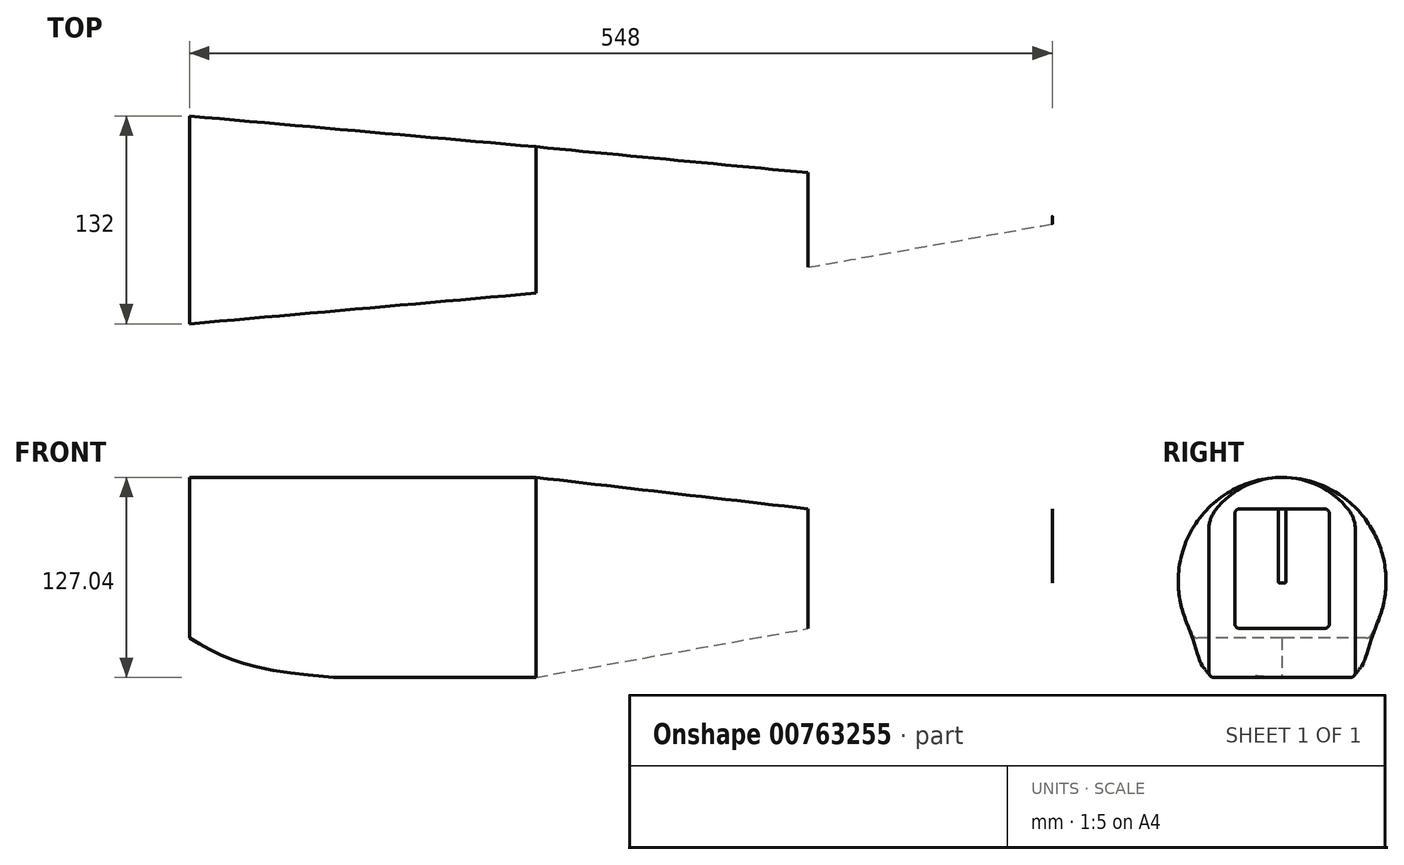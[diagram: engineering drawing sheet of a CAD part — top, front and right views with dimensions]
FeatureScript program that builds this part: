
annotation { "Feature Type Name" : "Feature", "Feature Type Description" : "" }
export const myFeature = defineFeature(function(context is Context, id is Id, definition is map)
    precondition{}
    {
        {
            var Q0;
            Q0=qCreatedBy(makeId("Front.planeOp"),FACE);
            var sketch = newSketch(context, id + "F0", { "sketchPlane" : qUnion([Q0])});
            skLineSegment(sketch, "E0", {"start": v(-298.93, 72.07) * mm, "end": v(-78.93, 72.07) * mm});
            skLineSegment(sketch, "E1", {"start": v(-298.93, 72.07) * mm, "end": v(-298.93, -29.93) * mm});
            skLineSegment(sketch, "E2", {"start": v(-78.93, 72.07) * mm, "end": v(-78.93, -54.93) * mm});
            skLineSegment(sketch, "E3", {"start": v(94.07, 52.07) * mm, "end": v(94.07, -23.93) * mm});
            skLineSegment(sketch, "E4", {"start": v(249.07, 52.07) * mm, "end": v(249.07, 5.07) * mm});
            skLineSegment(sketch, "E5", {"start": v(249.07, 5.07) * mm, "end": v(94.07, -23.93) * mm});
            skLineSegment(sketch, "E6", {"start": v(94.07, -23.93) * mm, "end": v(-78.93, -54.93) * mm});
            skLineSegment(sketch, "E7", {"start": v(-78.93, 72.07) * mm, "end": v(94.07, 52.07) * mm});
            skLineSegment(sketch, "E8", {"start": v(249.07, 52.07) * mm, "end": v(94.07, 52.07) * mm});
            skLineSegment(sketch, "E9", {"start": v(-78.93, 72.07) * mm, "end": v(94.07, 72.07) * mm, "construction": true});
            skLineSegment(sketch, "E10", {"start": v(94.07, 72.07) * mm, "end": v(249.07, 72.07) * mm, "construction": true});
            skLineSegment(sketch, "E11", {"start": v(94.07, 52.07) * mm, "end": v(94.07, 72.07) * mm, "construction": true});
            skLineSegment(sketch, "E12", {"start": v(249.07, 52.07) * mm, "end": v(249.07, 72.07) * mm, "construction": true});
            skLineSegment(sketch, "E13", {"start": v(-208.93, -54.93) * mm, "end": v(-208.93, -54.83) * mm, "construction": true});
            skFitSpline(sketch, "E14", {"points": [v(-298.93, -29.93) * mm, v(-277.86, -41.2) * mm, v(-246.75, -50.26) * mm, v(-207.1, -54.93) * mm, v(-204.2, -54.93) * mm, v(-200.61, -54.93) * mm, v(-196.68, -54.93) * mm, v(-192.58, -54.93) * mm, v(-78.93, -54.93) * mm], "startDerivative": vector(147.7, -86.05) * mm, "endDerivative": vector(505, 0.02) * mm});
            skLineSegment(sketch, "E15", {"start": v(-298.93, 6.07) * mm, "end": v(249.07, 6.07) * mm, "construction": true});
            skSolve(sketch);
        }
        {
            var Q0;
            Q0=sQuery(id+"F0.wireOp",EDGE,"E1");
            cPlane(context, id + "F1", {"entities" : qUnion([Q0]), "cplaneType" : CPlaneType.LINE_ANGLE, "offset" : 25 * mm, "angle" : 0 * degree, "width" : 150 * mm, "height" : 150 * mm});
        }
        {
            var Q0;
            Q0=sQuery(id+"F0.wireOp",EDGE,"E2");
            cPlane(context, id + "F2", {"entities" : qUnion([Q0]), "cplaneType" : CPlaneType.LINE_ANGLE, "offset" : 25 * mm, "angle" : 0 * degree, "width" : 150 * mm, "height" : 150 * mm});
        }
        {
            var Q0;
            Q0=sQuery(id+"F0.wireOp",EDGE,"E3");
            cPlane(context, id + "F3", {"entities" : qUnion([Q0]), "cplaneType" : CPlaneType.LINE_ANGLE, "offset" : 25 * mm, "angle" : 0 * degree, "width" : 150 * mm, "height" : 150 * mm});
        }
        {
            var Q0;
            Q0=qCreatedBy(id+"F1.planeOp",FACE);
            var sketch = newSketch(context, id + "F4", { "sketchPlane" : qUnion([Q0])});
            skArc(sketch, "E16", {"start": v(56.22, -28.5) * mm, "mid": v(42.66, 56.42) * mm, "end": v(-43.34, 55.84) * mm});
            skLineSegment(sketch, "E17", {"start": v(-53.67, -29.93) * mm, "end": v(53.67, -29.93) * mm});
            skPoint(sketch, "E18.visualSharp", {"position": v(55.32, -29.93) * mm});
            skArc(sketch, "E18.filletArc", {"start": v(53.67, -29.93) * mm, "mid": v(55.13, -29.55) * mm, "end": v(56.22, -28.5) * mm});
            skPoint(sketch, "E19.visualSharp", {"position": v(-55.32, -29.93) * mm});
            skArc(sketch, "E19.filletArc", {"start": v(-56.22, -28.5) * mm, "mid": v(-55.13, -29.55) * mm, "end": v(-53.67, -29.93) * mm});
            skArc(sketch, "E20", {"start": v(-43.34, 55.84) * mm, "mid": v(-65.24, 16.03) * mm, "end": v(-56.22, -28.5) * mm});
            skArc(sketch, "E21.MirrorCS", {"start": v(43.34, 55.84) * mm, "mid": v(65.24, 16.03) * mm, "end": v(56.22, -28.5) * mm});
            skLineSegment(sketch, "E22", {"start": v(-66, 6.07) * mm, "end": v(66, 6.07) * mm, "construction": true});
            skSolve(sketch);
        }
        {
            var Q0;
            Q0=qCreatedBy(id+"F2.planeOp",FACE);
            var sketch = newSketch(context, id + "F5", { "sketchPlane" : qUnion([Q0])});
            skLineSegment(sketch, "E23.top", {"start": v(43.5, -54.93) * mm, "end": v(-43.5, -54.93) * mm});
            skLineSegment(sketch, "E23.left", {"start": v(46.5, 39.09) * mm, "end": v(46.5, -51.93) * mm});
            skLineSegment(sketch, "E23.right", {"start": v(-46.5, 39.09) * mm, "end": v(-46.5, -51.93) * mm});
            skPoint(sketch, "E23.middle", {"position": v(0, -4.93) * mm});
            skArc(sketch, "E24", {"start": v(42.3, 51.35) * mm, "mid": v(0, 72.07) * mm, "end": v(-42.3, 51.35) * mm});
            skPoint(sketch, "E25.visualSharp", {"position": v(46.5, 45.07) * mm});
            skArc(sketch, "E25.filletArc", {"start": v(46.5, 39.09) * mm, "mid": v(45.42, 45.57) * mm, "end": v(42.3, 51.35) * mm});
            skPoint(sketch, "E26.visualSharp", {"position": v(46.5, -54.93) * mm});
            skArc(sketch, "E26.filletArc", {"start": v(43.5, -54.93) * mm, "mid": v(45.62, -54.06) * mm, "end": v(46.5, -51.93) * mm});
            skPoint(sketch, "E27.visualSharp", {"position": v(-46.5, -54.93) * mm});
            skArc(sketch, "E27.filletArc", {"start": v(-46.5, -51.93) * mm, "mid": v(-45.62, -54.06) * mm, "end": v(-43.5, -54.93) * mm});
            skPoint(sketch, "E28.visualSharp", {"position": v(-46.5, 45.07) * mm});
            skArc(sketch, "E28.filletArc", {"start": v(-42.3, 51.35) * mm, "mid": v(-45.42, 45.57) * mm, "end": v(-46.5, 39.09) * mm});
            skLineSegment(sketch, "E29", {"start": v(46.5, 6.07) * mm, "end": v(-46.5, 6.07) * mm, "construction": true});
            skSolve(sketch);
        }
        {
            var Q0;
            Q0=qCreatedBy(id+"F3.planeOp",FACE);
            var sketch = newSketch(context, id + "F6", { "sketchPlane" : qUnion([Q0])});
            skLineSegment(sketch, "E30.bottom", {"start": v(27, 52.07) * mm, "end": v(-27, 52.07) * mm});
            skLineSegment(sketch, "E30.top", {"start": v(27, -23.93) * mm, "end": v(-27, -23.93) * mm});
            skLineSegment(sketch, "E30.left", {"start": v(30, 49.07) * mm, "end": v(30, -20.93) * mm});
            skLineSegment(sketch, "E30.right", {"start": v(-30, 49.07) * mm, "end": v(-30, -20.93) * mm});
            skPoint(sketch, "E30.middle", {"position": v(0, 14.07) * mm});
            skPoint(sketch, "E31.visualSharp", {"position": v(30, 52.07) * mm});
            skArc(sketch, "E31.filletArc", {"start": v(30, 49.07) * mm, "mid": v(29.12, 51.19) * mm, "end": v(27, 52.07) * mm});
            skPoint(sketch, "E32.visualSharp", {"position": v(-30, 52.07) * mm});
            skArc(sketch, "E32.filletArc", {"start": v(-27, 52.07) * mm, "mid": v(-29.12, 51.19) * mm, "end": v(-30, 49.07) * mm});
            skPoint(sketch, "E33.visualSharp", {"position": v(30, -23.93) * mm});
            skArc(sketch, "E33.filletArc", {"start": v(27, -23.93) * mm, "mid": v(29.12, -23.06) * mm, "end": v(30, -20.93) * mm});
            skPoint(sketch, "E34.visualSharp", {"position": v(-30, -23.93) * mm});
            skArc(sketch, "E34.filletArc", {"start": v(-30, -20.93) * mm, "mid": v(-29.12, -23.06) * mm, "end": v(-27, -23.93) * mm});
            skLineSegment(sketch, "E35", {"start": v(30, 6.07) * mm, "end": v(-30, 6.07) * mm, "construction": true});
            skSolve(sketch);
        }
        {
            var Q0;
            Q0=sQuery(id+"F0.wireOp",EDGE,"E4");
            cPlane(context, id + "F7", {"entities" : qUnion([Q0]), "cplaneType" : CPlaneType.LINE_ANGLE, "offset" : 25 * mm, "angle" : 0 * degree, "width" : 150 * mm, "height" : 150 * mm});
        }
        {
            var Q0;
            Q0=qCreatedBy(id+"F7.planeOp",FACE);
            var sketch = newSketch(context, id + "F8", { "sketchPlane" : qUnion([Q0])});
            skLineSegment(sketch, "E36.bottom", {"start": v(1.5, 5.07) * mm, "end": v(-1.5, 5.07) * mm});
            skLineSegment(sketch, "E36.top", {"start": v(1.5, 52.07) * mm, "end": v(-1.5, 52.07) * mm});
            skLineSegment(sketch, "E36.right", {"start": v(-2.5, 6.07) * mm, "end": v(-2.5, 51.07) * mm});
            skPoint(sketch, "E36.middle", {"position": v(0, 28.57) * mm});
            skLineSegment(sketch, "E37", {"start": v(2.5, 6.07) * mm, "end": v(2.5, 51.07) * mm});
            skLineSegment(sketch, "E38", {"start": v(2.5, 6.07) * mm, "end": v(-2.5, 6.07) * mm, "construction": true});
            skPoint(sketch, "E39.visualSharp", {"position": v(2.5, 52.07) * mm});
            skArc(sketch, "E39.filletArc", {"start": v(2.5, 51.07) * mm, "mid": v(2.2, 51.77) * mm, "end": v(1.5, 52.07) * mm});
            skPoint(sketch, "E40.visualSharp", {"position": v(-2.5, 52.07) * mm});
            skArc(sketch, "E40.filletArc", {"start": v(-1.5, 52.07) * mm, "mid": v(-2.2, 51.77) * mm, "end": v(-2.5, 51.07) * mm});
            skPoint(sketch, "E41.visualSharp", {"position": v(2.5, 5.07) * mm});
            skArc(sketch, "E41.filletArc", {"start": v(1.5, 5.07) * mm, "mid": v(2.2, 5.36) * mm, "end": v(2.5, 6.07) * mm});
            skPoint(sketch, "E42.visualSharp", {"position": v(-2.5, 5.07) * mm});
            skArc(sketch, "E42.filletArc", {"start": v(-2.5, 6.07) * mm, "mid": v(-2.2, 5.36) * mm, "end": v(-1.5, 5.07) * mm});
            skSolve(sketch);
        }
        {
            var Q0;
            Q0=sQuery(id+"F0.wireOp",EDGE,"E15");
            cPlane(context, id + "F9", {"entities" : qUnion([Q0]), "cplaneType" : CPlaneType.LINE_ANGLE, "offset" : 25 * mm, "angle" : 90 * degree, "width" : 150 * mm, "height" : 150 * mm});
        }
        {
            var Q0;
            Q0=qCreatedBy(id+"F9.planeOp",FACE);
            var sketch = newSketch(context, id + "F10", { "sketchPlane" : qUnion([Q0])});
            skLineSegment(sketch, "E43", {"start": v(-298.93, -66) * mm, "end": v(-78.93, -46.5) * mm});
            skLineSegment(sketch, "E44.MirrorCS", {"start": v(-298.93, 66) * mm, "end": v(-78.93, 46.5) * mm});
            skPoint(sketch, "E45.orphan", {"position": v(249.07, -2.5) * mm});
            skPoint(sketch, "E46.end.orphan", {"position": v(249.07, 2.5) * mm});
            skPoint(sketch, "E47.MirrorCS.start.orphan", {"position": v(-78.93, -46.5) * mm});
            skLineSegment(sketch, "E48", {"start": v(-78.93, 46.5) * mm, "end": v(94.07, 30) * mm});
            skLineSegment(sketch, "E49", {"start": v(94.07, 30) * mm, "end": v(249.07, 2.5) * mm});
            skLineSegment(sketch, "E50.MirrorCS", {"start": v(-78.93, -46.5) * mm, "end": v(94.07, -30) * mm});
            skLineSegment(sketch, "E51.MirrorCS", {"start": v(94.07, -30) * mm, "end": v(249.07, -2.5) * mm});
            skSolve(sketch);
        }
        {
            var Q0;
            Q0=makeQuery(id+"F4.imprint","IMPRINT",FACE,{"disambiguationData":[TD([[makeQuery(id+"F4.imprint","IMPRINT",EDGE,{"derivedFrom":sQuery(id+"F4.wireOp",EDGE,"E16")}),1.0]])]});
            var Q1;
            Q1=makeQuery(id+"F5.imprint","IMPRINT",FACE,{"disambiguationData":[TD([[makeQuery(id+"F5.imprint","IMPRINT",EDGE,{"derivedFrom":sQuery(id+"F5.wireOp",EDGE,"E23.top")}),-1.0]])]});
            var Q2;
            Q2=sQuery(id+"F0.wireOp",EDGE,"E0");
            var Q3;
            Q3=sQuery(id+"F0.wireOp",EDGE,"E14");
            var Q4;
            Q4=sQuery(id+"F10.wireOp",EDGE,"E44.MirrorCS");
            var Q5;
            Q5=sQuery(id+"F10.wireOp",EDGE,"E43");
            loft(context, id + "F11", {"addGuides" : true, "sheetProfilesArray" : [{ "sheetProfileEntities" : qUnion([Q0]) }, { "sheetProfileEntities" : qUnion([Q1]) }], "guidesArray" : [{ "guideEntities" : qUnion([Q2]), "guideDerivativeType" : LoftGuideDerivativeType.DEFAULT, "guideDerivativeMagnitude" : 1 }, { "guideEntities" : qUnion([Q3]), "guideDerivativeType" : LoftGuideDerivativeType.DEFAULT, "guideDerivativeMagnitude" : 1 }, { "guideEntities" : qUnion([Q4]), "guideDerivativeType" : LoftGuideDerivativeType.DEFAULT, "guideDerivativeMagnitude" : 1 }, { "guideEntities" : qUnion([Q5]), "guideDerivativeType" : LoftGuideDerivativeType.DEFAULT, "guideDerivativeMagnitude" : 1 }]});
        }
        {
            var Q1;
            Q1=makeQuery(id+"F5.imprint","IMPRINT",FACE,{"disambiguationData":[TD([[makeQuery(id+"F5.imprint","IMPRINT",EDGE,{"derivedFrom":sQuery(id+"F5.wireOp",EDGE,"E23.top")}),-1.0]])]});
            var Q2;
            Q2=makeQuery(id+"F6.imprint","IMPRINT",FACE,{"disambiguationData":[TD([[makeQuery(id+"F6.imprint","IMPRINT",EDGE,{"derivedFrom":sQuery(id+"F6.wireOp",EDGE,"E30.bottom")}),1.0]])]});
            var Q3;
            Q3=sQuery(id+"F10.wireOp",EDGE,"E48");
            var Q4;
            Q4=sQuery(id+"F0.wireOp",EDGE,"E6");
            var Q5;
            Q5=sQuery(id+"F10.wireOp",EDGE,"E50.MirrorCS");
            var Q6;
            Q6=sQuery(id+"F0.wireOp",EDGE,"E7");
            loft(context, id + "F12", {"operationType" : NewBodyOperationType.ADD, "addGuides" : true, "sheetProfilesArray" : [{ "sheetProfileEntities" : qUnion([Q1]) }, { "sheetProfileEntities" : qUnion([Q2]) }], "guidesArray" : [{ "guideEntities" : qUnion([Q3]), "guideDerivativeType" : LoftGuideDerivativeType.DEFAULT, "guideDerivativeMagnitude" : 1 }, { "guideEntities" : qUnion([Q4]), "guideDerivativeType" : LoftGuideDerivativeType.DEFAULT, "guideDerivativeMagnitude" : 1 }, { "guideEntities" : qUnion([Q5]), "guideDerivativeType" : LoftGuideDerivativeType.DEFAULT, "guideDerivativeMagnitude" : 1 }, { "guideEntities" : qUnion([Q6]), "guideDerivativeType" : LoftGuideDerivativeType.DEFAULT, "guideDerivativeMagnitude" : 1 }]});
        }
        {
            var Q1;
            Q1=makeQuery(id+"F6.imprint","IMPRINT",FACE,{"disambiguationData":[TD([[makeQuery(id+"F6.imprint","IMPRINT",EDGE,{"derivedFrom":sQuery(id+"F6.wireOp",EDGE,"E30.bottom")}),1.0]])]});
            var Q2;
            Q2=makeQuery(id+"F8.imprint","IMPRINT",FACE,{"disambiguationData":[TD([[makeQuery(id+"F8.imprint","IMPRINT",EDGE,{"derivedFrom":sQuery(id+"F8.wireOp",EDGE,"E36.bottom")}),-1.0]])]});
            var Q3;
            Q3=sQuery(id+"F0.wireOp",EDGE,"E8");
            var Q4;
            Q4=sQuery(id+"F0.wireOp",EDGE,"E5");
            var Q5;
            Q5=sQuery(id+"F10.wireOp",EDGE,"E51.MirrorCS");
            var Q6;
            Q6=sQuery(id+"F10.wireOp",EDGE,"E49");
            loft(context, id + "F13", {"operationType" : NewBodyOperationType.ADD, "addGuides" : true, "sheetProfilesArray" : [{ "sheetProfileEntities" : qUnion([Q1]) }, { "sheetProfileEntities" : qUnion([Q2]) }], "guidesArray" : [{ "guideEntities" : qUnion([Q3]), "guideDerivativeType" : LoftGuideDerivativeType.DEFAULT, "guideDerivativeMagnitude" : 1 }, { "guideEntities" : qUnion([Q4]), "guideDerivativeType" : LoftGuideDerivativeType.DEFAULT, "guideDerivativeMagnitude" : 1 }, { "guideEntities" : qUnion([Q5]), "guideDerivativeType" : LoftGuideDerivativeType.DEFAULT, "guideDerivativeMagnitude" : 1 }, { "guideEntities" : qUnion([Q6]), "guideDerivativeType" : LoftGuideDerivativeType.DEFAULT, "guideDerivativeMagnitude" : 1 }]});
        }
    });
